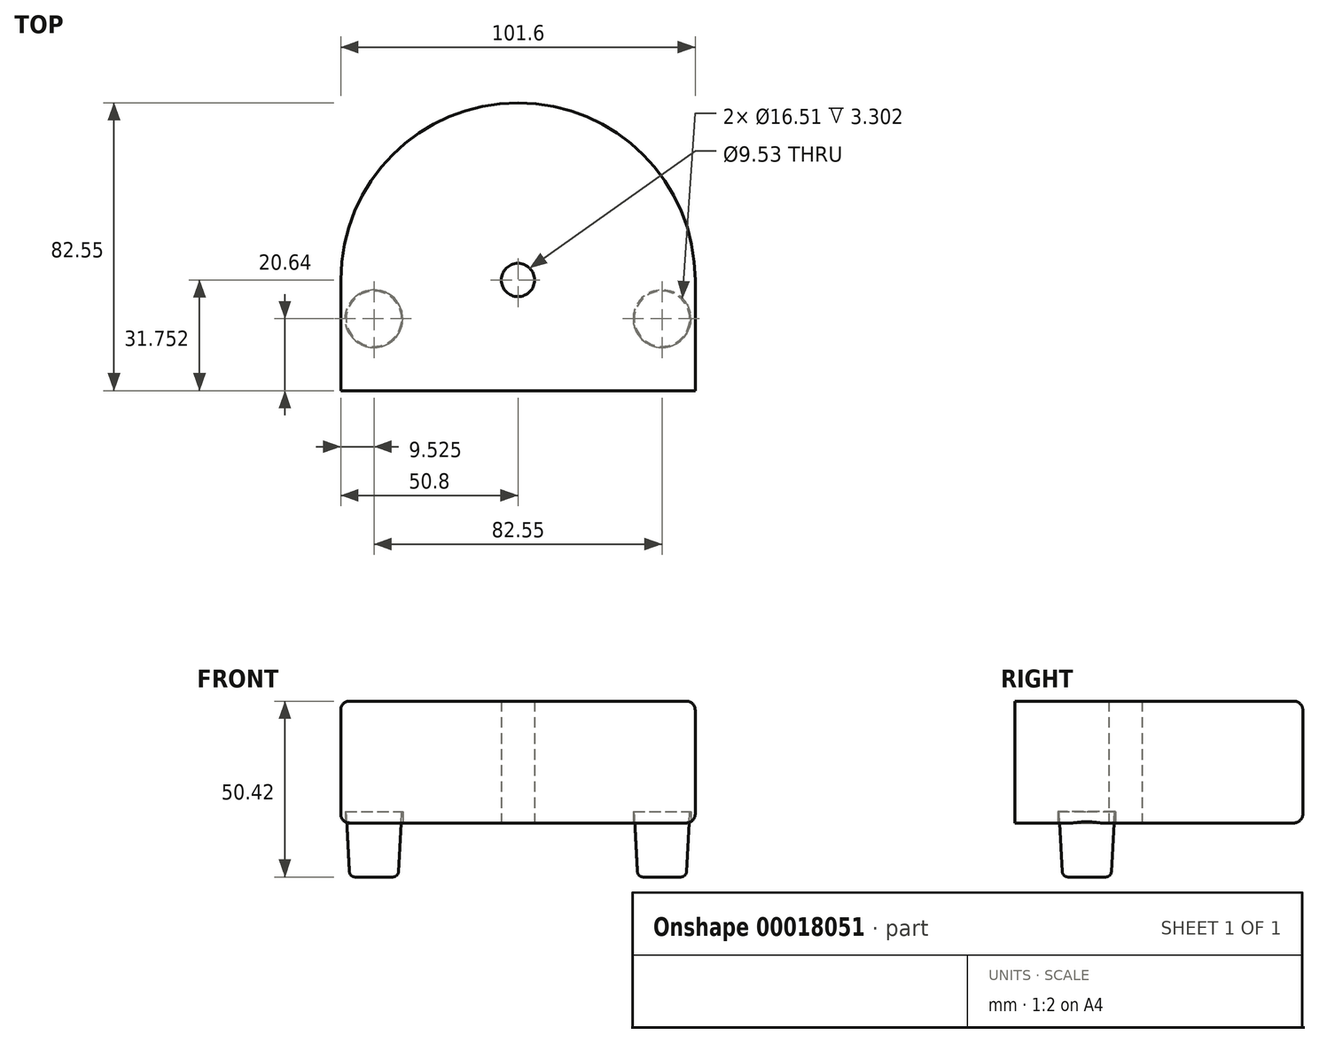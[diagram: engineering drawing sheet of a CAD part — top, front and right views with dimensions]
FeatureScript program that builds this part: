
annotation { "Feature Type Name" : "Feature", "Feature Type Description" : "" }
export const myFeature = defineFeature(function(context is Context, id is Id, definition is map)
    precondition{}
    {
        {
            var Q0;
            Q0=qCreatedBy(makeId("Top.planeOp"),FACE);
            var sketch = newSketch(context, id + "F0", { "sketchPlane" : qUnion([Q0])});
            skLineSegment(sketch, "E0.rect.bottom", {"start": v(50.8, -39.69) * mm, "end": v(-50.8, -39.69) * mm});
            skPoint(sketch, "E0.rect.middle", {"position": v(0, 0) * mm});
            skArc(sketch, "E1", {"start": v(50.8, -7.94) * mm, "mid": v(0, 42.86) * mm, "end": v(-50.8, -7.94) * mm});
            skLineSegment(sketch, "E2", {"start": v(-50.8, -39.69) * mm, "end": v(-50.8, -7.94) * mm});
            skLineSegment(sketch, "E3", {"start": v(50.8, -39.69) * mm, "end": v(50.8, -7.94) * mm});
            skCircle(sketch, "E4", {"center": v(0, -7.94) * mm, "radius": 4.76 * mm});
            skSolve(sketch);
        }
        {
            var Q0;
            Q0=makeQuery(id+"F0.imprint","IMPRINT",FACE,{"disambiguationData":[TD([[makeQuery(id+"F0.imprint","IMPRINT",EDGE,{"derivedFrom":sQuery(id+"F0.wireOp",EDGE,"E0.rect.bottom")}),-1.0]])]});
            extrude(context, id + "F1", {"entities" : qUnion([Q0]), "endBound" : BoundingType.SYMMETRIC, "depth" : 34.92 * mm});
        }
        {
            var Q0;
            Q0=makeQuery(id+"F1.opExtrude","CAP_EDGE",EDGE,{"disambiguationData":[OSD([sQuery(id+"F0.wireOp",EDGE,"E2")])],"isStart":false});
            var Q1;
            Q1=makeQuery(id+"F1.opExtrude","CAP_EDGE",EDGE,{"disambiguationData":[OSD([sQuery(id+"F0.wireOp",EDGE,"E1")])],"isStart":false});
            var Q2;
            Q2=makeQuery(id+"F1.opExtrude","CAP_EDGE",EDGE,{"disambiguationData":[OSD([sQuery(id+"F0.wireOp",EDGE,"E2")])],"isStart":true});
            var Q3;
            Q3=makeQuery(id+"F1.opExtrude","CAP_EDGE",EDGE,{"disambiguationData":[OSD([sQuery(id+"F0.wireOp",EDGE,"E1")])],"isStart":true});
            var Q4;
            Q4=makeQuery(id+"F1.opExtrude","CAP_EDGE",EDGE,{"disambiguationData":[OSD([sQuery(id+"F0.wireOp",EDGE,"E3")])],"isStart":true});
            var Q5;
            Q5=makeQuery(id+"F1.opExtrude","CAP_EDGE",EDGE,{"disambiguationData":[OSD([sQuery(id+"F0.wireOp",EDGE,"E3")])],"isStart":false});
            fillet(context, id + "F2", {"entities" : qUnion([Q0, Q1, Q2, Q3, Q4, Q5]), "radius" : 2.54 * mm, "tangentPropagation" : true, "allowEdgeOverflow" : false});
        }
        {
            var Q0;
            Q0=makeQuery(id+"F1.opExtrude","CAP_FACE",FACE,{"disambiguationData":[OSD([sQuery(id+"F0.wireOp",EDGE,"E0.rect.bottom"),sQuery(id+"F0.wireOp",EDGE,"E1"),sQuery(id+"F0.wireOp",EDGE,"E2"),sQuery(id+"F0.wireOp",EDGE,"E3"),sQuery(id+"F0.wireOp",EDGE,"E4")])],"isStart":true});
            var sketch = newSketch(context, id + "F3", { "sketchPlane" : qUnion([Q0])});
            skLineSegment(sketch, "E5", {"start": v(-41.28, 19.05) * mm, "end": v(41.28, 19.05) * mm, "construction": true});
            skCircle(sketch, "E6", {"center": v(-41.28, 19.05) * mm, "radius": 8.26 * mm});
            skCircle(sketch, "E7", {"center": v(41.28, 19.05) * mm, "radius": 8.26 * mm});
            skPoint(sketch, "E8", {"position": v(0, 7.94) * mm});
            skLineSegment(sketch, "E9", {"start": v(0, 7.94) * mm, "end": v(0, 19.05) * mm, "construction": true});
            skSolve(sketch);
        }
        {
            var Q0;
            Q0 = qSketchRegion(id + "F3", true);
            extrude(context, id + "F4", {"entities" : qUnion([Q0]), "operationType" : NewBodyOperationType.REMOVE, "oppositeDirection" : true, "depth" : 3.3 * mm});
        }
        {
            var Q0;
            Q0=makeQuery(id+"F4.boolean.opBoolean","COPY",FACE,{"derivedFrom":makeQuery(id+"F4.opExtrude","CAP_FACE",FACE,{"disambiguationData":[OSD([sQuery(id+"F3.wireOp",EDGE,"E6")])],"isStart":false})});
            var sketch = newSketch(context, id + "F5", { "sketchPlane" : qUnion([Q0])});
            skCircle(sketch, "E10", {"center": v(-41.28, 19.05) * mm, "radius": 7.94 * mm});
            skCircle(sketch, "E11", {"center": v(41.28, 19.05) * mm, "radius": 7.94 * mm});
            skLineSegment(sketch, "E12", {"start": v(-41.28, 19.05) * mm, "end": v(41.28, 19.05) * mm, "construction": true});
            skSolve(sketch);
        }
        {
            var Q0;
            Q0 = qSketchRegion(id + "F5", true);
            extrude(context, id + "F6", {"entities" : qUnion([Q0]), "operationType" : NewBodyOperationType.ADD, "depth" : 18.8 * mm, "hasDraft" : true, "draftAngle" : 3 * degree, "draftPullDirection" : true});
        }
        {
            var Q0;
            Q0=makeQuery(id+"F6.opExtrude","CAP_EDGE",EDGE,{"disambiguationData":[OSD([sQuery(id+"F5.wireOp",EDGE,"E10")])],"isStart":false});
            var Q1;
            Q1=makeQuery(id+"F6.opExtrude","CAP_EDGE",EDGE,{"disambiguationData":[OSD([sQuery(id+"F5.wireOp",EDGE,"E11")])],"isStart":false});
            fillet(context, id + "F7", {"entities" : qUnion([Q0, Q1]), "radius" : 1.59 * mm, "tangentPropagation" : true, "allowEdgeOverflow" : false});
        }
    });
